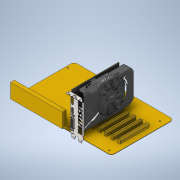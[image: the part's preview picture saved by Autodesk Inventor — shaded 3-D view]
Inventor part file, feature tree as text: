
AUTODESK INVENTOR PART (.ipt)
format: ipt  version: 2021 (Build 250183000, 183)  size: 10,106,368 bytes
history: mixed  units: in
note: dims shown in document units (in); Inventor stores cm internally (conversion verified against a paired STEP export)
features: other x5, extrude x1, fillet x1, sketch x1, imported_body x1
ambient origin geometry x8: Origin, YZ Plane, XZ Plane, XY Plane, X Axis, Y Axis, Z Axis, Center Point
bodies: Solid1 (imported_parasolid)
feature tree (9):
  other  "MotherboardGPU.iam"
  other  "ATX MODEL.ipt:1"
  other  "msi_rx560.ipt:1"
  extrude  "Extrusion1"  Depth=0.39in TaperAngle=0.0deg
  fillet  "Fillet1"  Radius=0.39in
  other  "Srf1"
  sketch  "Sketch1"  dims[d0=0.3937in d1=2.1in d2=0.0in d3=0.39in]
  other  "Srf1::Derived"
  imported_body  NMx_Import_Brep_tag  [imported B-rep: ~37 faces, bbox_mm=[189.5196, 94.228464, 192.639223]]
